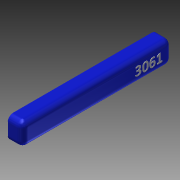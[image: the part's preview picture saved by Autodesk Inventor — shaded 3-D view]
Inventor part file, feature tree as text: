
AUTODESK INVENTOR PART (.ipt)
format: ipt  version: 2013 (Build 170138000, 138)  size: 378,368 bytes
history: native  units: in
note: dims shown in document units (in); Inventor stores cm internally (conversion verified against a paired STEP export)
features: reference x7, extrude x4, sketch x3, fillet x1, projected_geometry x1
ambient origin geometry x8: Origin, YZ Plane, XZ Plane, XY Plane, X Axis, Y Axis, Z Axis, Center Point
bodies: Solid1 (feature_tree)
feature tree (16):
  sketch  "Sketch1"  dims[d0=0.0625in d1=0.0in d3=1.0in]
  extrude  "Extrusion1"  Depth=1.0in
  extrude  "Extrusion2"  Depth=0.0625in
  extrude  "Extrusion3"  Depth=0.0625in TaperAngle=0.0deg
  fillet  "Fillet1"  Radius=1.3125in
  extrude  "Extrusion5"  Depth=0.0625in
  reference  "Reference4"
  reference  "Reference5"
  sketch  "Sketch2"  dims[d7=1.0in d9=0.0625in]
  reference  "Reference6"
  reference  "Reference7"
  reference  "Reference8"
  reference  "Reference9"
  reference  "Reference10"
  projected_geometry  "Projected Loop1"
  sketch  "Sketch4"  dims[d10=34.0in d11=0.0in d12=0.0625in d13=0.0in d14=1.3125in d20=0.0625in d21=0.0625in d26=1.0in d27=6.0in d28=2.5in d29=0.0625in d30=0.0in]
